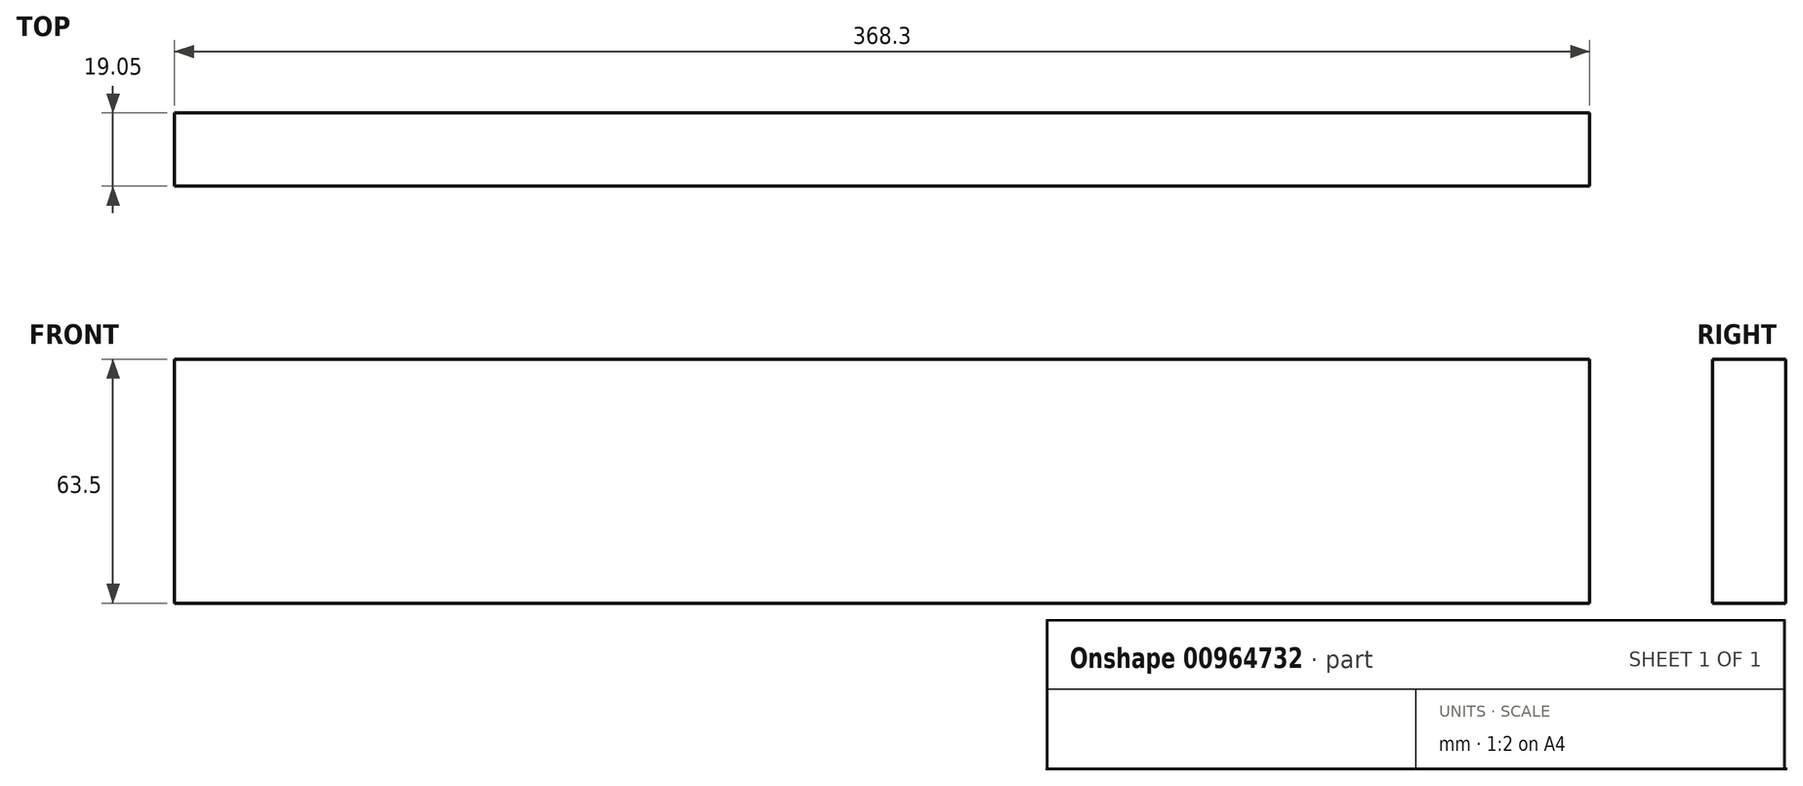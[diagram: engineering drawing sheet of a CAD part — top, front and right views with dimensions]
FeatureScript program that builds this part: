
annotation { "Feature Type Name" : "Feature", "Feature Type Description" : "" }
export const myFeature = defineFeature(function(context is Context, id is Id, definition is map)
    precondition{}
    {
        {
            var Q0;
            Q0=qCreatedBy(makeId("Front.planeOp"),FACE);
            var sketch = newSketch(context, id + "F0", { "sketchPlane" : qUnion([Q0])});
            skLineSegment(sketch, "E0.bottom", {"start": v(0, 0) * mm, "end": v(-368.3, 0) * mm});
            skLineSegment(sketch, "E0.top", {"start": v(0, 63.5) * mm, "end": v(-368.3, 63.5) * mm});
            skLineSegment(sketch, "E0.left", {"start": v(0, 0) * mm, "end": v(0, 63.5) * mm});
            skLineSegment(sketch, "E0.right", {"start": v(-368.3, 0) * mm, "end": v(-368.3, 63.5) * mm});
            skSolve(sketch);
        }
        {
            var Q0;
            Q0 = qSketchRegion(id + "F0", true);
            extrude(context, id + "F1", {"entities" : qUnion([Q0]), "depth" : 19.05 * mm, "offsetDistance" : 25.4 * mm});
        }
    });
